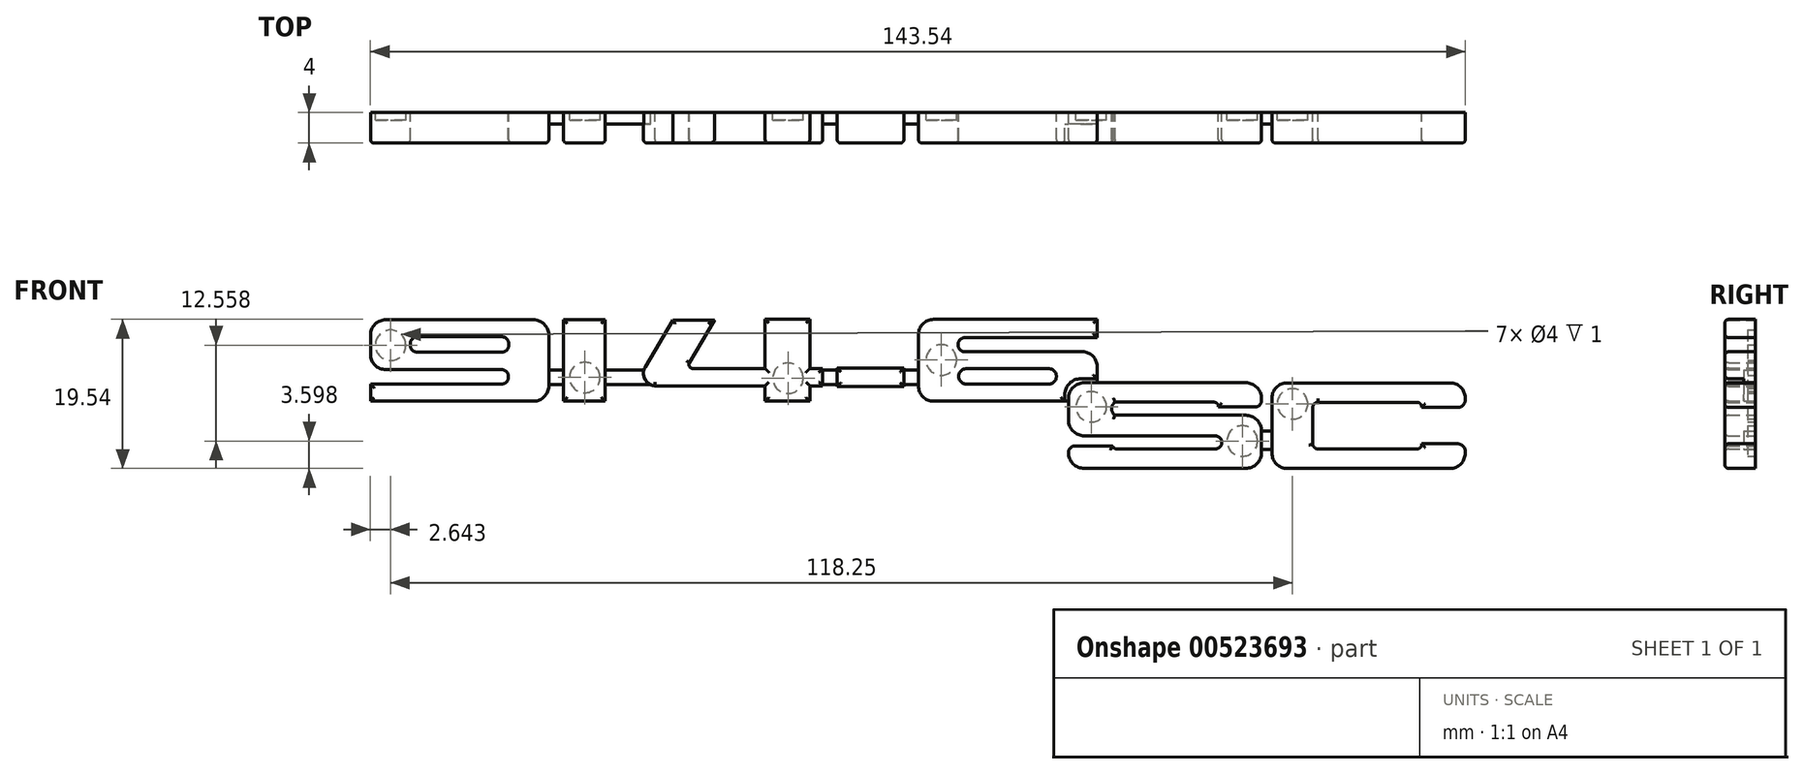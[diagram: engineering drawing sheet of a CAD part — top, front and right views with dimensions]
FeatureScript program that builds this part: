
annotation { "Feature Type Name" : "Feature", "Feature Type Description" : "" }
export const myFeature = defineFeature(function(context is Context, id is Id, definition is map)
    precondition{}
    {
        {
            var Q0;
            Q0=qCreatedBy(makeId("Front.planeOp"),FACE);
            var sketch = newSketch(context, id + "F0", { "sketchPlane" : qUnion([Q0])});
            skLineSegment(sketch, "E0.bottom", {"start": v(-66.52, 34.25) * mm, "end": v(-47.14, 34.25) * mm});
            skLineSegment(sketch, "E0.top", {"start": v(-68.52, 23.57) * mm, "end": v(-47.14, 23.57) * mm});
            skLineSegment(sketch, "E0.left", {"start": v(-68.52, 32.25) * mm, "end": v(-68.52, 29.72) * mm});
            skLineSegment(sketch, "E0.right", {"start": v(-45.14, 32.25) * mm, "end": v(-45.14, 25.57) * mm});
            skPoint(sketch, "E1.visualSharp", {"position": v(-68.52, 34.25) * mm});
            skArc(sketch, "E1.filletArc", {"start": v(-66.52, 34.25) * mm, "mid": v(-67.93, 33.67) * mm, "end": v(-68.52, 32.25) * mm});
            skLineSegment(sketch, "E2", {"start": v(-66.52, 27.72) * mm, "end": v(-51.34, 27.72) * mm});
            skLineSegment(sketch, "E3", {"start": v(-50.44, 26.81) * mm, "end": v(-50.44, 26.71) * mm});
            skLineSegment(sketch, "E4", {"start": v(-51.34, 25.81) * mm, "end": v(-68.52, 25.81) * mm});
            skLineSegment(sketch, "E5.bottom", {"start": v(-62.39, 32.02) * mm, "end": v(-51.29, 32.02) * mm});
            skLineSegment(sketch, "E5.top", {"start": v(-62.39, 30) * mm, "end": v(-51.29, 30) * mm});
            skLineSegment(sketch, "E5.left", {"start": v(-63.3, 31.12) * mm, "end": v(-63.3, 30.91) * mm});
            skLineSegment(sketch, "E5.right", {"start": v(-50.39, 31.12) * mm, "end": v(-50.39, 30.91) * mm});
            skLineSegment(sketch, "E6.trimOffspring", {"start": v(-68.52, 25.81) * mm, "end": v(-68.52, 23.57) * mm});
            skPoint(sketch, "E7.visualSharp", {"position": v(-68.52, 27.72) * mm});
            skArc(sketch, "E7.filletArc", {"start": v(-68.52, 29.72) * mm, "mid": v(-67.93, 28.3) * mm, "end": v(-66.52, 27.72) * mm});
            skPoint(sketch, "E8.visualSharp", {"position": v(-50.44, 27.72) * mm});
            skArc(sketch, "E8.filletArc", {"start": v(-50.44, 26.81) * mm, "mid": v(-50.7, 27.45) * mm, "end": v(-51.34, 27.72) * mm});
            skPoint(sketch, "E9.visualSharp", {"position": v(-50.44, 25.81) * mm});
            skArc(sketch, "E9.filletArc", {"start": v(-51.34, 25.81) * mm, "mid": v(-50.7, 26.08) * mm, "end": v(-50.44, 26.71) * mm});
            skPoint(sketch, "E10.visualSharp", {"position": v(-63.3, 32.02) * mm});
            skArc(sketch, "E10.filletArc", {"start": v(-62.39, 32.02) * mm, "mid": v(-63.03, 31.75) * mm, "end": v(-63.3, 31.12) * mm});
            skPoint(sketch, "E11.visualSharp", {"position": v(-63.3, 30) * mm});
            skArc(sketch, "E11.filletArc", {"start": v(-63.3, 30.91) * mm, "mid": v(-63.03, 30.27) * mm, "end": v(-62.39, 30) * mm});
            skPoint(sketch, "E12.visualSharp", {"position": v(-50.39, 32.02) * mm});
            skArc(sketch, "E12.filletArc", {"start": v(-50.39, 31.12) * mm, "mid": v(-50.65, 31.75) * mm, "end": v(-51.29, 32.02) * mm});
            skPoint(sketch, "E13.visualSharp", {"position": v(-50.39, 30) * mm});
            skArc(sketch, "E13.filletArc", {"start": v(-51.29, 30) * mm, "mid": v(-50.65, 30.27) * mm, "end": v(-50.39, 30.91) * mm});
            skPoint(sketch, "E14.visualSharp", {"position": v(-45.14, 34.25) * mm});
            skArc(sketch, "E14.filletArc", {"start": v(-45.14, 32.25) * mm, "mid": v(-45.72, 33.67) * mm, "end": v(-47.14, 34.25) * mm});
            skPoint(sketch, "E15.visualSharp", {"position": v(-45.14, 23.57) * mm});
            skArc(sketch, "E15.filletArc", {"start": v(-47.14, 23.57) * mm, "mid": v(-45.72, 24.16) * mm, "end": v(-45.14, 25.57) * mm});
            skLineSegment(sketch, "E16.bottom", {"start": v(-43.22, 34.26) * mm, "end": v(-37.74, 34.26) * mm});
            skLineSegment(sketch, "E16.top", {"start": v(-43.22, 23.58) * mm, "end": v(-37.74, 23.58) * mm});
            skLineSegment(sketch, "E16.left", {"start": v(-43.22, 34.26) * mm, "end": v(-43.22, 23.58) * mm});
            skLineSegment(sketch, "E16.right", {"start": v(-37.74, 34.26) * mm, "end": v(-37.74, 23.58) * mm});
            skLineSegment(sketch, "E17.bottom", {"start": v(-10.91, 34.3) * mm, "end": v(-16.77, 34.3) * mm});
            skLineSegment(sketch, "E17.top", {"start": v(-10.91, 23.58) * mm, "end": v(-16.77, 23.58) * mm});
            skLineSegment(sketch, "E17.left", {"start": v(-10.91, 34.3) * mm, "end": v(-10.91, 27.87) * mm});
            skLineSegment(sketch, "E17.right", {"start": v(-16.77, 34.3) * mm, "end": v(-16.77, 27.87) * mm});
            skLineSegment(sketch, "E18.bottom", {"start": v(-9.22, 27.87) * mm, "end": v(-10.91, 27.87) * mm});
            skLineSegment(sketch, "E18.top", {"start": v(-9.22, 25.6) * mm, "end": v(-10.91, 25.6) * mm});
            skLineSegment(sketch, "E18.left", {"start": v(-9.22, 27.87) * mm, "end": v(-9.22, 25.6) * mm});
            skLineSegment(sketch, "E19.trimOffspring", {"start": v(-16.77, 27.87) * mm, "end": v(-26.26, 27.87) * mm});
            skLineSegment(sketch, "E20.trimOffspring", {"start": v(-10.91, 25.6) * mm, "end": v(-10.91, 23.58) * mm});
            skLineSegment(sketch, "E21.trimOffspring", {"start": v(-16.77, 25.6) * mm, "end": v(-26.26, 25.6) * mm});
            skLineSegment(sketch, "E22.trimOffspring", {"start": v(-16.77, 25.6) * mm, "end": v(-16.77, 23.58) * mm});
            skLineSegment(sketch, "E23", {"start": v(-23.37, 34.22) * mm, "end": v(-28.86, 34.22) * mm});
            skLineSegment(sketch, "E24", {"start": v(-23.37, 34.22) * mm, "end": v(-26.68, 28.6) * mm});
            skLineSegment(sketch, "E25", {"start": v(-28.86, 34.22) * mm, "end": v(-32.5, 28.07) * mm});
            skLineSegment(sketch, "E26", {"start": v(-26.26, 25.6) * mm, "end": v(-31.22, 25.6) * mm});
            skArc(sketch, "E27", {"start": v(-32.5, 28.07) * mm, "mid": v(-32.54, 26.48) * mm, "end": v(-31.22, 25.6) * mm});
            skArc(sketch, "E28", {"start": v(-26.68, 28.6) * mm, "mid": v(-26.69, 28.12) * mm, "end": v(-26.26, 27.87) * mm});
            skLineSegment(sketch, "E29.bottom", {"start": v(-7.32, 27.9) * mm, "end": v(1.42, 27.9) * mm});
            skLineSegment(sketch, "E29.top", {"start": v(-7.32, 25.5) * mm, "end": v(1.42, 25.5) * mm});
            skLineSegment(sketch, "E29.left", {"start": v(-7.32, 27.9) * mm, "end": v(-7.32, 25.5) * mm});
            skLineSegment(sketch, "E29.right", {"start": v(1.42, 27.9) * mm, "end": v(1.42, 25.5) * mm});
            skLineSegment(sketch, "E30.bottom", {"start": v(26.75, 34.3) * mm, "end": v(5.33, 34.3) * mm});
            skLineSegment(sketch, "E30.top", {"start": v(22.52, 23.57) * mm, "end": v(5.33, 23.57) * mm});
            skLineSegment(sketch, "E30.left", {"start": v(26.75, 34.3) * mm, "end": v(26.75, 31.9) * mm});
            skLineSegment(sketch, "E30.right", {"start": v(3.33, 32.3) * mm, "end": v(3.33, 25.57) * mm});
            skPoint(sketch, "E31.visualSharp", {"position": v(3.33, 34.3) * mm});
            skArc(sketch, "E31.filletArc", {"start": v(5.33, 34.3) * mm, "mid": v(3.91, 33.71) * mm, "end": v(3.33, 32.3) * mm});
            skPoint(sketch, "E32.visualSharp", {"position": v(3.33, 23.57) * mm});
            skArc(sketch, "E32.filletArc", {"start": v(3.33, 25.57) * mm, "mid": v(3.91, 24.16) * mm, "end": v(5.33, 23.57) * mm});
            skLineSegment(sketch, "E33", {"start": v(26.75, 31.9) * mm, "end": v(9.44, 31.9) * mm});
            skLineSegment(sketch, "E34", {"start": v(9.44, 30.06) * mm, "end": v(24.83, 30.06) * mm});
            skLineSegment(sketch, "E35.bottom", {"start": v(9.61, 27.84) * mm, "end": v(20.42, 27.84) * mm});
            skLineSegment(sketch, "E35.top", {"start": v(9.61, 25.82) * mm, "end": v(20.42, 25.82) * mm});
            skLineSegment(sketch, "E35.left", {"start": v(8.61, 26.84) * mm, "end": v(8.61, 26.82) * mm});
            skLineSegment(sketch, "E35.right", {"start": v(21.42, 26.84) * mm, "end": v(21.42, 26.82) * mm});
            skPoint(sketch, "E36.visualSharp", {"position": v(8.61, 27.84) * mm});
            skArc(sketch, "E36.filletArc", {"start": v(9.61, 27.84) * mm, "mid": v(8.9, 27.54) * mm, "end": v(8.61, 26.84) * mm});
            skPoint(sketch, "E37.visualSharp", {"position": v(8.61, 25.82) * mm});
            skArc(sketch, "E37.filletArc", {"start": v(8.61, 26.82) * mm, "mid": v(8.9, 26.12) * mm, "end": v(9.61, 25.82) * mm});
            skPoint(sketch, "E38.visualSharp", {"position": v(27.42, 23.74) * mm});
            skArc(sketch, "E38.filletArc", {"start": v(21.42, 26.84) * mm, "mid": v(21.13, 27.54) * mm, "end": v(20.42, 27.84) * mm});
            skPoint(sketch, "E39.visualSharp", {"position": v(21.5, 24.83) * mm});
            skArc(sketch, "E39.filletArc", {"start": v(20.42, 25.82) * mm, "mid": v(21.13, 26.12) * mm, "end": v(21.42, 26.82) * mm});
            skArc(sketch, "E40", {"start": v(9.44, 31.9) * mm, "mid": v(8.52, 30.98) * mm, "end": v(9.44, 30.06) * mm});
            skLineSegment(sketch, "E41.trimOffspring", {"start": v(26.75, 28.14) * mm, "end": v(26.75, 26.52) * mm});
            skPoint(sketch, "E42.visualSharp", {"position": v(26.75, 30.06) * mm});
            skArc(sketch, "E42.filletArc", {"start": v(26.75, 28.14) * mm, "mid": v(26.19, 29.5) * mm, "end": v(24.83, 30.06) * mm});
            skLineSegment(sketch, "E43", {"start": v(22.52, 23.57) * mm, "end": v(22.52, 24.42) * mm});
            skLineSegment(sketch, "E44", {"start": v(24.62, 26.52) * mm, "end": v(26.75, 26.52) * mm});
            skPoint(sketch, "E45.visualSharp", {"position": v(22.6, 25.53) * mm});
            skArc(sketch, "E45.filletArc", {"start": v(24.62, 26.52) * mm, "mid": v(23.13, 25.9) * mm, "end": v(22.52, 24.42) * mm});
            skPoint(sketch, "E46.firstSnap0", {"position": v(21.13, 26.12) * mm});
            skLineSegment(sketch, "E46.bottom", {"start": v(46.22, 26) * mm, "end": v(40.34, 26) * mm});
            skLineSegment(sketch, "E46.top", {"start": v(46.22, 14.76) * mm, "end": v(40.34, 14.76) * mm});
            skLineSegment(sketch, "E46.left", {"start": v(48.32, 23.9) * mm, "end": v(48.32, 23.65) * mm});
            skLineSegment(sketch, "E46.right", {"start": v(23, 23.9) * mm, "end": v(23, 21.11) * mm});
            skPoint(sketch, "E47.visualSharp", {"position": v(23, 26) * mm});
            skArc(sketch, "E47.filletArc", {"start": v(25.1, 26) * mm, "mid": v(23.61, 25.38) * mm, "end": v(23, 23.9) * mm});
            skPoint(sketch, "E48.visualSharp", {"position": v(22.6, 11.98) * mm});
            skArc(sketch, "E48.filletArc", {"start": v(48.32, 23.9) * mm, "mid": v(47.7, 25.38) * mm, "end": v(46.22, 26) * mm});
            skPoint(sketch, "E49.visualSharp", {"position": v(49.1, 15.16) * mm});
            skArc(sketch, "E49.filletArc", {"start": v(46.22, 14.76) * mm, "mid": v(47.7, 15.37) * mm, "end": v(48.32, 16.86) * mm});
            skPoint(sketch, "E50.visualSharp", {"position": v(23, 14.76) * mm});
            skArc(sketch, "E50.filletArc", {"start": v(23, 16.86) * mm, "mid": v(23.61, 15.37) * mm, "end": v(25.1, 14.76) * mm});
            skLineSegment(sketch, "E51", {"start": v(25.08, 19.03) * mm, "end": v(30.91, 19.03) * mm});
            skLineSegment(sketch, "E52", {"start": v(42.24, 17.3) * mm, "end": v(40.34, 17.3) * mm});
            skLineSegment(sketch, "E53", {"start": v(28.8, 17.7) * mm, "end": v(23.84, 17.7) * mm});
            skLineSegment(sketch, "E54", {"start": v(29.07, 21.73) * mm, "end": v(30.91, 21.73) * mm});
            skLineSegment(sketch, "E55", {"start": v(47.48, 22.82) * mm, "end": v(42.67, 22.82) * mm});
            skLineSegment(sketch, "E56", {"start": v(42.07, 23.45) * mm, "end": v(40.34, 23.45) * mm});
            skArc(sketch, "E57", {"start": v(29.1, 23.45) * mm, "mid": v(28.67, 22.6) * mm, "end": v(29.07, 21.73) * mm});
            skPoint(sketch, "E58.end.orphan", {"position": v(42.67, 23.45) * mm});
            skArc(sketch, "E59", {"start": v(42.67, 22.82) * mm, "mid": v(42.5, 23.26) * mm, "end": v(42.07, 23.45) * mm});
            skArc(sketch, "E60", {"start": v(28.8, 17.7) * mm, "mid": v(29.01, 17.41) * mm, "end": v(29.35, 17.3) * mm});
            skLineSegment(sketch, "E61.trimOffspring", {"start": v(23, 16.86) * mm, "end": v(23, 16.85) * mm});
            skPoint(sketch, "E62.visualSharp", {"position": v(23, 17.7) * mm});
            skArc(sketch, "E62.filletArc", {"start": v(23.84, 17.7) * mm, "mid": v(23.25, 17.45) * mm, "end": v(23, 16.85) * mm});
            skPoint(sketch, "E63.visualSharp", {"position": v(23, 19.03) * mm});
            skArc(sketch, "E63.filletArc", {"start": v(23, 21.11) * mm, "mid": v(23.6, 19.64) * mm, "end": v(25.08, 19.03) * mm});
            skLineSegment(sketch, "E64.trimOffspring", {"start": v(48.32, 19.65) * mm, "end": v(48.32, 16.86) * mm});
            skPoint(sketch, "E65.visualSharp", {"position": v(49.1, 22.93) * mm});
            skArc(sketch, "E65.filletArc", {"start": v(47.48, 22.82) * mm, "mid": v(48.07, 23.06) * mm, "end": v(48.32, 23.65) * mm});
            skPoint(sketch, "E66.visualSharp", {"position": v(49.1, 21.7) * mm});
            skArc(sketch, "E66.filletArc", {"start": v(48.32, 19.65) * mm, "mid": v(47.7, 21.12) * mm, "end": v(46.24, 21.73) * mm});
            skLineSegment(sketch, "E67.bottom", {"start": v(51.66, 25.98) * mm, "end": v(57.41, 25.98) * mm});
            skLineSegment(sketch, "E67.top", {"start": v(51.66, 14.76) * mm, "end": v(57.41, 14.76) * mm});
            skLineSegment(sketch, "E67.left", {"start": v(49.68, 24) * mm, "end": v(49.68, 16.74) * mm});
            skLineSegment(sketch, "E68.bottom", {"start": v(68.68, 23.43) * mm, "end": v(66.84, 23.43) * mm});
            skLineSegment(sketch, "E68.top", {"start": v(68.69, 17.3) * mm, "end": v(66.84, 17.3) * mm});
            skLineSegment(sketch, "E69", {"start": v(55.03, 18) * mm, "end": v(55.03, 22.74) * mm});
            skArc(sketch, "E70", {"start": v(69.32, 22.74) * mm, "mid": v(69.15, 23.22) * mm, "end": v(68.68, 23.43) * mm});
            skPoint(sketch, "E71.visualSharp", {"position": v(75.02, 17.93) * mm});
            skPoint(sketch, "E72.visualSharp", {"position": v(75.02, 14.93) * mm});
            skArc(sketch, "E72.filletArc", {"start": v(73.04, 14.76) * mm, "mid": v(74.44, 15.34) * mm, "end": v(75.02, 16.74) * mm});
            skPoint(sketch, "E73.visualSharp", {"position": v(48.52, 12.25) * mm});
            skArc(sketch, "E73.filletArc", {"start": v(75.02, 24) * mm, "mid": v(74.44, 25.4) * mm, "end": v(73.04, 25.98) * mm});
            skPoint(sketch, "E74.visualSharp", {"position": v(23.18, 12.25) * mm});
            skArc(sketch, "E74.filletArc", {"start": v(51.66, 25.98) * mm, "mid": v(50.26, 25.4) * mm, "end": v(49.68, 24) * mm});
            skPoint(sketch, "E75.visualSharp", {"position": v(49.68, 14.76) * mm});
            skArc(sketch, "E75.filletArc", {"start": v(49.68, 16.74) * mm, "mid": v(50.26, 15.34) * mm, "end": v(51.66, 14.76) * mm});
            skArc(sketch, "E76", {"start": v(55.72, 23.43) * mm, "mid": v(55.23, 23.23) * mm, "end": v(55.03, 22.74) * mm});
            skLineSegment(sketch, "E77", {"start": v(55.03, 18) * mm, "end": v(55.03, 17.88) * mm});
            skArc(sketch, "E78", {"start": v(55.03, 17.88) * mm, "mid": v(55.27, 17.47) * mm, "end": v(55.72, 17.3) * mm});
            skLineSegment(sketch, "E79.bottom", {"start": v(3.33, 27.64) * mm, "end": v(1.42, 27.64) * mm});
            skLineSegment(sketch, "E79.top", {"start": v(3.33, 25.76) * mm, "end": v(1.42, 25.76) * mm});
            skLineSegment(sketch, "E79.left", {"start": v(3.33, 27.64) * mm, "end": v(3.33, 25.76) * mm});
            skLineSegment(sketch, "E80.trimOffspring", {"start": v(-7.32, 27.64) * mm, "end": v(-9.22, 27.64) * mm});
            skLineSegment(sketch, "E81.trimOffspring", {"start": v(-7.32, 25.76) * mm, "end": v(-9.22, 25.76) * mm});
            skLineSegment(sketch, "E82", {"start": v(-31.8, 25.76) * mm, "end": v(-33.56, 25.76) * mm});
            skLineSegment(sketch, "E83", {"start": v(-32.67, 27.64) * mm, "end": v(-33.56, 27.64) * mm});
            skLineSegment(sketch, "E84", {"start": v(-33.56, 27.64) * mm, "end": v(-37.74, 27.64) * mm});
            skLineSegment(sketch, "E85", {"start": v(-33.56, 25.76) * mm, "end": v(-37.74, 25.76) * mm});
            skLineSegment(sketch, "E86.trimOffspring", {"start": v(-43.22, 27.64) * mm, "end": v(-45.14, 27.64) * mm});
            skLineSegment(sketch, "E87.trimOffspring", {"start": v(-43.22, 25.76) * mm, "end": v(-45.14, 25.76) * mm});
            skPoint(sketch, "E88.end.orphan", {"position": v(49.68, 19.46) * mm});
            skPoint(sketch, "E89.end.orphan", {"position": v(49.68, 17.09) * mm});
            skArc(sketch, "E90", {"start": v(42.24, 17.3) * mm, "mid": v(43.1, 18.17) * mm, "end": v(42.24, 19.03) * mm});
            skLineSegment(sketch, "E91.top", {"start": v(69.32, 18) * mm, "end": v(74.02, 18) * mm});
            skArc(sketch, "E92", {"start": v(68.69, 17.3) * mm, "mid": v(69.15, 17.51) * mm, "end": v(69.32, 18) * mm});
            skPoint(sketch, "E93.trimOffspring.start.orphan", {"position": v(75.02, 17.07) * mm});
            skLineSegment(sketch, "E94", {"start": v(75.02, 16.74) * mm, "end": v(75.02, 17) * mm});
            skLineSegment(sketch, "E95", {"start": v(69.32, 22.74) * mm, "end": v(74.02, 22.74) * mm});
            skLineSegment(sketch, "E96", {"start": v(75.02, 24) * mm, "end": v(75.02, 23.74) * mm});
            skPoint(sketch, "E97.visualSharp", {"position": v(75.02, 22.74) * mm});
            skArc(sketch, "E97.filletArc", {"start": v(74.02, 22.74) * mm, "mid": v(74.73, 23.04) * mm, "end": v(75.02, 23.74) * mm});
            skPoint(sketch, "E98.visualSharp", {"position": v(75.02, 18) * mm});
            skArc(sketch, "E98.filletArc", {"start": v(75.02, 17) * mm, "mid": v(74.73, 17.7) * mm, "end": v(74.02, 18) * mm});
            skLineSegment(sketch, "E99.trimOffspring", {"start": v(30.91, 26) * mm, "end": v(25.1, 26) * mm});
            skLineSegment(sketch, "E100.trimOffspring", {"start": v(30.91, 23.45) * mm, "end": v(29.1, 23.45) * mm});
            skLineSegment(sketch, "E101.trimOffspring", {"start": v(40.34, 21.73) * mm, "end": v(46.24, 21.73) * mm});
            skLineSegment(sketch, "E102.trimOffspring", {"start": v(40.34, 19.03) * mm, "end": v(42.24, 19.03) * mm});
            skLineSegment(sketch, "E103.trimOffspring", {"start": v(30.91, 17.3) * mm, "end": v(29.35, 17.3) * mm});
            skLineSegment(sketch, "E104.trimOffspring", {"start": v(30.91, 14.76) * mm, "end": v(25.1, 14.76) * mm});
            skLineSegment(sketch, "E105.trimOffspring", {"start": v(66.84, 25.98) * mm, "end": v(73.04, 25.98) * mm});
            skLineSegment(sketch, "E106.trimOffspring", {"start": v(57.41, 23.43) * mm, "end": v(55.72, 23.43) * mm});
            skLineSegment(sketch, "E107.trimOffspring", {"start": v(57.41, 17.3) * mm, "end": v(55.72, 17.3) * mm});
            skLineSegment(sketch, "E108.trimOffspring", {"start": v(66.84, 14.76) * mm, "end": v(73.04, 14.76) * mm});
            skLineSegment(sketch, "E109", {"start": v(30.91, 26) * mm, "end": v(40.34, 26) * mm});
            skLineSegment(sketch, "E110", {"start": v(30.91, 23.45) * mm, "end": v(40.34, 23.45) * mm});
            skLineSegment(sketch, "E111", {"start": v(30.91, 21.73) * mm, "end": v(40.34, 21.73) * mm});
            skLineSegment(sketch, "E112", {"start": v(30.91, 19.03) * mm, "end": v(40.34, 19.03) * mm});
            skLineSegment(sketch, "E113", {"start": v(30.91, 17.3) * mm, "end": v(40.34, 17.3) * mm});
            skLineSegment(sketch, "E114", {"start": v(30.91, 14.76) * mm, "end": v(40.34, 14.76) * mm});
            skLineSegment(sketch, "E115", {"start": v(57.41, 25.98) * mm, "end": v(66.84, 25.98) * mm});
            skLineSegment(sketch, "E116", {"start": v(57.41, 23.43) * mm, "end": v(66.84, 23.43) * mm});
            skLineSegment(sketch, "E117", {"start": v(57.41, 17.3) * mm, "end": v(66.84, 17.3) * mm});
            skLineSegment(sketch, "E118", {"start": v(57.41, 14.76) * mm, "end": v(66.84, 14.76) * mm});
            skLineSegment(sketch, "E119", {"start": v(26.75, 26.52) * mm, "end": v(26.75, 26) * mm});
            skLineSegment(sketch, "E120", {"start": v(22.52, 23.57) * mm, "end": v(23, 23.57) * mm});
            skLineSegment(sketch, "E121", {"start": v(48.32, 17.24) * mm, "end": v(49.68, 17.24) * mm});
            skLineSegment(sketch, "E122", {"start": v(48.32, 19.65) * mm, "end": v(49.68, 19.65) * mm});
            skSolve(sketch);
        }
        {
            var Q0;
            {var subQ0=sQuery(id+"F0.wireOp",EDGE,"E86.trimOffspring");Q0=makeQuery(id+"F0.imprint","IMPRINT",FACE,{"disambiguationData":[TD([[makeQuery(id+"F0.imprint","IMPRINT",EDGE,{"derivedFrom":subQ0}),1.0]])]});}
            var Q1;
            {var subQ1=sQuery(id+"F0.wireOp",EDGE,"E82");Q1=makeQuery(id+"F0.imprint","IMPRINT",FACE,{"disambiguationData":[TD([[makeQuery(id+"F0.imprint","IMPRINT",EDGE,{"derivedFrom":subQ1}),-1.0]])]});}
            var Q2;
            {var subQ0=sQuery(id+"F0.wireOp",EDGE,"E80.trimOffspring");Q2=makeQuery(id+"F0.imprint","IMPRINT",FACE,{"disambiguationData":[TD([[makeQuery(id+"F0.imprint","IMPRINT",EDGE,{"derivedFrom":subQ0}),1.0]])]});}
            var Q3;
            {var subQ0=sQuery(id+"F0.wireOp",EDGE,"E79.bottom");Q3=makeQuery(id+"F0.imprint","IMPRINT",FACE,{"disambiguationData":[TD([[makeQuery(id+"F0.imprint","IMPRINT",EDGE,{"derivedFrom":subQ0}),1.0]])]});}
            var Q4;
            Q4=makeQuery(id+"F0.imprint","IMPRINT",FACE,{"disambiguationData":[TD([[makeQuery(id+"F0.imprint","IMPRINT",EDGE,{"derivedFrom":sQuery(id+"F0.wireOp",EDGE,"E64.trimOffspring")}),1.0]])]});
            var Q5;
            Q5=makeQuery(id+"F0.imprint","IMPRINT",FACE,{"disambiguationData":[TD([[makeQuery(id+"F0.imprint","IMPRINT",EDGE,{"derivedFrom":sQuery(id+"F0.wireOp",EDGE,"E43")}),-1.0]])]});
            extrude(context, id + "F1", {"entities" : qUnion([Q0, Q1, Q2, Q3, Q4, Q5]), "depth" : 1.5 * mm, "offsetDistance" : 25 * mm});
        }
        {
            var Q0;
            Q0=makeQuery(id+"F0.imprint","IMPRINT",FACE,{"disambiguationData":[TD([[makeQuery(id+"F0.imprint","IMPRINT",EDGE,{"derivedFrom":sQuery(id+"F0.wireOp",EDGE,"E0.bottom")}),-1.0]])]});
            var Q1;
            {var subQ3=sQuery(id+"F0.wireOp",EDGE,"E16.bottom");Q1=makeQuery(id+"F0.imprint","IMPRINT",FACE,{"disambiguationData":[TD([[makeQuery(id+"F0.imprint","IMPRINT",EDGE,{"derivedFrom":subQ3}),-1.0]])]});}
            var Q2;
            Q2=makeQuery(id+"F0.imprint","IMPRINT",FACE,{"disambiguationData":[TD([[makeQuery(id+"F0.imprint","IMPRINT",EDGE,{"derivedFrom":sQuery(id+"F0.wireOp",EDGE,"E17.bottom")}),1.0]])]});
            var Q3;
            {var subQ3=sQuery(id+"F0.wireOp",EDGE,"E29.bottom");Q3=makeQuery(id+"F0.imprint","IMPRINT",FACE,{"disambiguationData":[TD([[makeQuery(id+"F0.imprint","IMPRINT",EDGE,{"derivedFrom":subQ3}),-1.0]])]});}
            var Q4;
            Q4=makeQuery(id+"F0.imprint","IMPRINT",FACE,{"disambiguationData":[TD([[makeQuery(id+"F0.imprint","IMPRINT",EDGE,{"derivedFrom":sQuery(id+"F0.wireOp",EDGE,"E30.bottom")}),1.0]])]});
            var Q5;
            Q5=makeQuery(id+"F0.imprint","IMPRINT",FACE,{"disambiguationData":[TD([[makeQuery(id+"F0.imprint","IMPRINT",EDGE,{"derivedFrom":sQuery(id+"F0.wireOp",EDGE,"E46.top")}),-1.0]])]});
            var Q6;
            Q6=makeQuery(id+"F0.imprint","IMPRINT",FACE,{"disambiguationData":[TD([[makeQuery(id+"F0.imprint","IMPRINT",EDGE,{"derivedFrom":sQuery(id+"F0.wireOp",EDGE,"E67.bottom")}),-1.0]])]});
            extrude(context, id + "F2", {"entities" : qUnion([Q0, Q1, Q2, Q3, Q4, Q5, Q6]), "depth" : 4 * mm, "offsetDistance" : 25 * mm});
        }
        {
            var Q0;
            Q0=makeQuery(id+"F1.opExtrude","SWEPT_BODY",BODY,{"disambiguationData":[OSD([sQuery(id+"F0.wireOp",EDGE,"E0.right"),sQuery(id+"F0.wireOp",EDGE,"E16.left"),sQuery(id+"F0.wireOp",EDGE,"E86.trimOffspring"),sQuery(id+"F0.wireOp",EDGE,"E87.trimOffspring")])]});
            var Q1;
            Q1=makeQuery(id+"F1.opExtrude","SWEPT_BODY",BODY,{"disambiguationData":[OSD([sQuery(id+"F0.wireOp",EDGE,"E16.right"),sQuery(id+"F0.wireOp",EDGE,"E27"),sQuery(id+"F0.wireOp",EDGE,"E82"),sQuery(id+"F0.wireOp",EDGE,"E83"),sQuery(id+"F0.wireOp",EDGE,"E84"),sQuery(id+"F0.wireOp",EDGE,"E85")])]});
            var Q2;
            Q2=makeQuery(id+"F1.opExtrude","SWEPT_BODY",BODY,{"disambiguationData":[OSD([sQuery(id+"F0.wireOp",EDGE,"E18.left"),sQuery(id+"F0.wireOp",EDGE,"E29.left"),sQuery(id+"F0.wireOp",EDGE,"E80.trimOffspring"),sQuery(id+"F0.wireOp",EDGE,"E81.trimOffspring")])]});
            var Q3;
            Q3=makeQuery(id+"F1.opExtrude","SWEPT_BODY",BODY,{"disambiguationData":[OSD([sQuery(id+"F0.wireOp",EDGE,"E29.right"),sQuery(id+"F0.wireOp",EDGE,"E79.bottom"),sQuery(id+"F0.wireOp",EDGE,"E79.top"),sQuery(id+"F0.wireOp",EDGE,"E79.left")])]});
            var Q4;
            Q4=makeQuery(id+"F1.opExtrude","SWEPT_BODY",BODY,{"disambiguationData":[OSD([sQuery(id+"F0.wireOp",EDGE,"E43"),sQuery(id+"F0.wireOp",EDGE,"E44"),sQuery(id+"F0.wireOp",EDGE,"E45.filletArc"),sQuery(id+"F0.wireOp",EDGE,"E46.bottom"),sQuery(id+"F0.wireOp",EDGE,"E46.right"),sQuery(id+"F0.wireOp",EDGE,"E47.filletArc"),sQuery(id+"F0.wireOp",EDGE,"XMzfFIXU-IzKp-9okF-d4nS-TtUoLVSPwyGc"),sQuery(id+"F0.wireOp",EDGE,"e7Qd8Rkx-YhGh-OuG7-C6sY-1t4VXorSgqZP")])]});
            var Q5;
            Q5=makeQuery(id+"F1.opExtrude","SWEPT_BODY",BODY,{"disambiguationData":[OSD([sQuery(id+"F0.wireOp",EDGE,"E64.trimOffspring"),sQuery(id+"F0.wireOp",EDGE,"E67.left"),sQuery(id+"F0.wireOp",EDGE,"E89"),sQuery(id+"F0.wireOp",EDGE,"E88")])]});
            var Q6;
            Q6=makeQuery(id+"F2.opExtrude","SWEPT_BODY",BODY,{"disambiguationData":[OSD([sQuery(id+"F0.wireOp",EDGE,"E0.bottom"),sQuery(id+"F0.wireOp",EDGE,"E0.top"),sQuery(id+"F0.wireOp",EDGE,"E0.left"),sQuery(id+"F0.wireOp",EDGE,"E0.right"),sQuery(id+"F0.wireOp",EDGE,"E1.filletArc"),sQuery(id+"F0.wireOp",EDGE,"E2"),sQuery(id+"F0.wireOp",EDGE,"E3"),sQuery(id+"F0.wireOp",EDGE,"E4"),sQuery(id+"F0.wireOp",EDGE,"E5.bottom"),sQuery(id+"F0.wireOp",EDGE,"E5.top"),sQuery(id+"F0.wireOp",EDGE,"E5.left"),sQuery(id+"F0.wireOp",EDGE,"E5.right"),sQuery(id+"F0.wireOp",EDGE,"E6.trimOffspring"),sQuery(id+"F0.wireOp",EDGE,"E7.filletArc"),sQuery(id+"F0.wireOp",EDGE,"E8.filletArc"),sQuery(id+"F0.wireOp",EDGE,"E9.filletArc"),sQuery(id+"F0.wireOp",EDGE,"E10.filletArc"),sQuery(id+"F0.wireOp",EDGE,"E11.filletArc"),sQuery(id+"F0.wireOp",EDGE,"E12.filletArc"),sQuery(id+"F0.wireOp",EDGE,"E13.filletArc"),sQuery(id+"F0.wireOp",EDGE,"E14.filletArc"),sQuery(id+"F0.wireOp",EDGE,"E15.filletArc")])]});
            var Q7;
            Q7=makeQuery(id+"F2.opExtrude","SWEPT_BODY",BODY,{"disambiguationData":[OSD([sQuery(id+"F0.wireOp",EDGE,"E16.bottom"),sQuery(id+"F0.wireOp",EDGE,"E16.top"),sQuery(id+"F0.wireOp",EDGE,"E16.left"),sQuery(id+"F0.wireOp",EDGE,"E16.right")])]});
            var Q8;
            Q8=makeQuery(id+"F2.opExtrude","SWEPT_BODY",BODY,{"disambiguationData":[OSD([sQuery(id+"F0.wireOp",EDGE,"E17.bottom"),sQuery(id+"F0.wireOp",EDGE,"E17.top"),sQuery(id+"F0.wireOp",EDGE,"E17.left"),sQuery(id+"F0.wireOp",EDGE,"E17.right"),sQuery(id+"F0.wireOp",EDGE,"E18.bottom"),sQuery(id+"F0.wireOp",EDGE,"E18.top"),sQuery(id+"F0.wireOp",EDGE,"E18.left"),sQuery(id+"F0.wireOp",EDGE,"E19.trimOffspring"),sQuery(id+"F0.wireOp",EDGE,"E20.trimOffspring"),sQuery(id+"F0.wireOp",EDGE,"E21.trimOffspring"),sQuery(id+"F0.wireOp",EDGE,"E22.trimOffspring"),sQuery(id+"F0.wireOp",EDGE,"E23"),sQuery(id+"F0.wireOp",EDGE,"E24"),sQuery(id+"F0.wireOp",EDGE,"E25"),sQuery(id+"F0.wireOp",EDGE,"E26"),sQuery(id+"F0.wireOp",EDGE,"E27"),sQuery(id+"F0.wireOp",EDGE,"E28")])]});
            var Q9;
            Q9=makeQuery(id+"F2.opExtrude","SWEPT_BODY",BODY,{"disambiguationData":[OSD([sQuery(id+"F0.wireOp",EDGE,"E29.bottom"),sQuery(id+"F0.wireOp",EDGE,"E29.top"),sQuery(id+"F0.wireOp",EDGE,"E29.left"),sQuery(id+"F0.wireOp",EDGE,"E29.right")])]});
            var Q10;
            Q10=makeQuery(id+"F2.opExtrude","SWEPT_BODY",BODY,{"disambiguationData":[OSD([sQuery(id+"F0.wireOp",EDGE,"E30.bottom"),sQuery(id+"F0.wireOp",EDGE,"E30.top"),sQuery(id+"F0.wireOp",EDGE,"E30.left"),sQuery(id+"F0.wireOp",EDGE,"E30.right"),sQuery(id+"F0.wireOp",EDGE,"E31.filletArc"),sQuery(id+"F0.wireOp",EDGE,"E32.filletArc"),sQuery(id+"F0.wireOp",EDGE,"E33"),sQuery(id+"F0.wireOp",EDGE,"E34"),sQuery(id+"F0.wireOp",EDGE,"E35.bottom"),sQuery(id+"F0.wireOp",EDGE,"E35.top"),sQuery(id+"F0.wireOp",EDGE,"E35.left"),sQuery(id+"F0.wireOp",EDGE,"E35.right"),sQuery(id+"F0.wireOp",EDGE,"E36.filletArc"),sQuery(id+"F0.wireOp",EDGE,"E37.filletArc"),sQuery(id+"F0.wireOp",EDGE,"E38.filletArc"),sQuery(id+"F0.wireOp",EDGE,"E39.filletArc"),sQuery(id+"F0.wireOp",EDGE,"E40"),sQuery(id+"F0.wireOp",EDGE,"E41.trimOffspring"),sQuery(id+"F0.wireOp",EDGE,"E42.filletArc"),sQuery(id+"F0.wireOp",EDGE,"E43"),sQuery(id+"F0.wireOp",EDGE,"E44"),sQuery(id+"F0.wireOp",EDGE,"E45.filletArc"),sQuery(id+"F0.wireOp",EDGE,"E79.left")])]});
            var Q11;
            Q11=makeQuery(id+"F2.opExtrude","SWEPT_BODY",BODY,{"disambiguationData":[OSD([sQuery(id+"F0.wireOp",EDGE,"E46.bottom"),sQuery(id+"F0.wireOp",EDGE,"E46.top"),sQuery(id+"F0.wireOp",EDGE,"E46.left"),sQuery(id+"F0.wireOp",EDGE,"E46.right"),sQuery(id+"F0.wireOp",EDGE,"E47.filletArc"),sQuery(id+"F0.wireOp",EDGE,"E48.filletArc"),sQuery(id+"F0.wireOp",EDGE,"E49.filletArc"),sQuery(id+"F0.wireOp",EDGE,"E50.filletArc"),sQuery(id+"F0.wireOp",EDGE,"E51"),sQuery(id+"F0.wireOp",EDGE,"E52"),sQuery(id+"F0.wireOp",EDGE,"E53"),sQuery(id+"F0.wireOp",EDGE,"E54"),sQuery(id+"F0.wireOp",EDGE,"E55"),sQuery(id+"F0.wireOp",EDGE,"E56"),sQuery(id+"F0.wireOp",EDGE,"E57"),sQuery(id+"F0.wireOp",EDGE,"DLBRGIPo-igv8-U5Ki-hssD-qP5Wvc2arMu2"),sQuery(id+"F0.wireOp",EDGE,"E59"),sQuery(id+"F0.wireOp",EDGE,"E60"),sQuery(id+"F0.wireOp",EDGE,"E61.trimOffspring"),sQuery(id+"F0.wireOp",EDGE,"E62.filletArc"),sQuery(id+"F0.wireOp",EDGE,"E63.filletArc"),sQuery(id+"F0.wireOp",EDGE,"E64.trimOffspring"),sQuery(id+"F0.wireOp",EDGE,"E65.filletArc"),sQuery(id+"F0.wireOp",EDGE,"E66.filletArc")])]});
            var Q12;
            Q12=makeQuery(id+"F2.opExtrude","SWEPT_BODY",BODY,{"disambiguationData":[OSD([sQuery(id+"F0.wireOp",EDGE,"E67.bottom"),sQuery(id+"F0.wireOp",EDGE,"E67.top"),sQuery(id+"F0.wireOp",EDGE,"E67.left"),sQuery(id+"F0.wireOp",EDGE,"E67.right"),sQuery(id+"F0.wireOp",EDGE,"E68.bottom"),sQuery(id+"F0.wireOp",EDGE,"E68.top"),sQuery(id+"F0.wireOp",EDGE,"W34rrdPF-5A4v-98ez-cMOX-sxhZx3srIAKQ"),sQuery(id+"F0.wireOp",EDGE,"yoT0j4jh-KsDp-Vx2W-hgaE-VbdXvh3J3yn9"),sQuery(id+"F0.wireOp",EDGE,"E69"),sQuery(id+"F0.wireOp",EDGE,"E93.trimOffspring"),sQuery(id+"F0.wireOp",EDGE,"E70"),sQuery(id+"F0.wireOp",EDGE,"FAs5oKjp-0fME-HACK-cPX3-1Olh0WYhMQdt"),sQuery(id+"F0.wireOp",EDGE,"E71.filletArc"),sQuery(id+"F0.wireOp",EDGE,"E72.filletArc"),sQuery(id+"F0.wireOp",EDGE,"E73.filletArc"),sQuery(id+"F0.wireOp",EDGE,"E74.filletArc"),sQuery(id+"F0.wireOp",EDGE,"E75.filletArc"),sQuery(id+"F0.wireOp",EDGE,"E76"),sQuery(id+"F0.wireOp",EDGE,"E77"),sQuery(id+"F0.wireOp",EDGE,"E78")])]});
            booleanBodies(context, id + "F3", {"operationType" : BooleanOperationType.UNION, "tools" : qUnion([Q0, Q1, Q2, Q3, Q4, Q5, Q6, Q7, Q8, Q9, Q10, Q11, Q12])});
        }
        {
            var Q0;
            Q0=makeQuery(id+"F2.opExtrude","CAP_FACE",FACE,{"disambiguationData":[OSD([sQuery(id+"F0.wireOp",EDGE,"E0.bottom"),sQuery(id+"F0.wireOp",EDGE,"E0.top"),sQuery(id+"F0.wireOp",EDGE,"E0.left"),sQuery(id+"F0.wireOp",EDGE,"E0.right"),sQuery(id+"F0.wireOp",EDGE,"E1.filletArc"),sQuery(id+"F0.wireOp",EDGE,"E2"),sQuery(id+"F0.wireOp",EDGE,"E3"),sQuery(id+"F0.wireOp",EDGE,"E4"),sQuery(id+"F0.wireOp",EDGE,"E5.bottom"),sQuery(id+"F0.wireOp",EDGE,"E5.top"),sQuery(id+"F0.wireOp",EDGE,"E5.left"),sQuery(id+"F0.wireOp",EDGE,"E5.right"),sQuery(id+"F0.wireOp",EDGE,"E6.trimOffspring"),sQuery(id+"F0.wireOp",EDGE,"E7.filletArc"),sQuery(id+"F0.wireOp",EDGE,"E8.filletArc"),sQuery(id+"F0.wireOp",EDGE,"E9.filletArc"),sQuery(id+"F0.wireOp",EDGE,"E10.filletArc"),sQuery(id+"F0.wireOp",EDGE,"E11.filletArc"),sQuery(id+"F0.wireOp",EDGE,"E12.filletArc"),sQuery(id+"F0.wireOp",EDGE,"E13.filletArc"),sQuery(id+"F0.wireOp",EDGE,"E14.filletArc"),sQuery(id+"F0.wireOp",EDGE,"E15.filletArc")])],"isStart":false});
            var Q1;
            Q1=makeQuery(id+"F2.opExtrude","CAP_FACE",FACE,{"disambiguationData":[OSD([sQuery(id+"F0.wireOp",EDGE,"E16.bottom"),sQuery(id+"F0.wireOp",EDGE,"E16.top"),sQuery(id+"F0.wireOp",EDGE,"E16.left"),sQuery(id+"F0.wireOp",EDGE,"E16.right")])],"isStart":false});
            var Q2;
            Q2=makeQuery(id+"F2.opExtrude","CAP_FACE",FACE,{"disambiguationData":[OSD([sQuery(id+"F0.wireOp",EDGE,"E17.bottom"),sQuery(id+"F0.wireOp",EDGE,"E17.top"),sQuery(id+"F0.wireOp",EDGE,"E17.left"),sQuery(id+"F0.wireOp",EDGE,"E17.right"),sQuery(id+"F0.wireOp",EDGE,"E18.bottom"),sQuery(id+"F0.wireOp",EDGE,"E18.top"),sQuery(id+"F0.wireOp",EDGE,"E18.left"),sQuery(id+"F0.wireOp",EDGE,"E19.trimOffspring"),sQuery(id+"F0.wireOp",EDGE,"E20.trimOffspring"),sQuery(id+"F0.wireOp",EDGE,"E21.trimOffspring"),sQuery(id+"F0.wireOp",EDGE,"E22.trimOffspring"),sQuery(id+"F0.wireOp",EDGE,"E23"),sQuery(id+"F0.wireOp",EDGE,"E24"),sQuery(id+"F0.wireOp",EDGE,"E25"),sQuery(id+"F0.wireOp",EDGE,"E26"),sQuery(id+"F0.wireOp",EDGE,"E27"),sQuery(id+"F0.wireOp",EDGE,"E28")])],"isStart":false});
            var Q3;
            Q3=makeQuery(id+"F2.opExtrude","CAP_FACE",FACE,{"disambiguationData":[OSD([sQuery(id+"F0.wireOp",EDGE,"E29.bottom"),sQuery(id+"F0.wireOp",EDGE,"E29.top"),sQuery(id+"F0.wireOp",EDGE,"E29.left"),sQuery(id+"F0.wireOp",EDGE,"E29.right")])],"isStart":false});
            var Q4;
            Q4=makeQuery(id+"F2.opExtrude","CAP_FACE",FACE,{"disambiguationData":[OSD([sQuery(id+"F0.wireOp",EDGE,"E30.bottom"),sQuery(id+"F0.wireOp",EDGE,"E30.top"),sQuery(id+"F0.wireOp",EDGE,"E30.left"),sQuery(id+"F0.wireOp",EDGE,"E30.right"),sQuery(id+"F0.wireOp",EDGE,"E31.filletArc"),sQuery(id+"F0.wireOp",EDGE,"E32.filletArc"),sQuery(id+"F0.wireOp",EDGE,"E33"),sQuery(id+"F0.wireOp",EDGE,"E34"),sQuery(id+"F0.wireOp",EDGE,"E35.bottom"),sQuery(id+"F0.wireOp",EDGE,"E35.top"),sQuery(id+"F0.wireOp",EDGE,"E35.left"),sQuery(id+"F0.wireOp",EDGE,"E35.right"),sQuery(id+"F0.wireOp",EDGE,"E36.filletArc"),sQuery(id+"F0.wireOp",EDGE,"E37.filletArc"),sQuery(id+"F0.wireOp",EDGE,"E38.filletArc"),sQuery(id+"F0.wireOp",EDGE,"E39.filletArc"),sQuery(id+"F0.wireOp",EDGE,"E40"),sQuery(id+"F0.wireOp",EDGE,"E41.trimOffspring"),sQuery(id+"F0.wireOp",EDGE,"E42.filletArc"),sQuery(id+"F0.wireOp",EDGE,"E43"),sQuery(id+"F0.wireOp",EDGE,"E44"),sQuery(id+"F0.wireOp",EDGE,"E45.filletArc"),sQuery(id+"F0.wireOp",EDGE,"E79.left")])],"isStart":false});
            var Q5;
            Q5=makeQuery(id+"F2.opExtrude","CAP_FACE",FACE,{"disambiguationData":[OSD([sQuery(id+"F0.wireOp",EDGE,"E46.bottom"),sQuery(id+"F0.wireOp",EDGE,"E46.top"),sQuery(id+"F0.wireOp",EDGE,"E46.left"),sQuery(id+"F0.wireOp",EDGE,"E46.right"),sQuery(id+"F0.wireOp",EDGE,"E47.filletArc"),sQuery(id+"F0.wireOp",EDGE,"E48.filletArc"),sQuery(id+"F0.wireOp",EDGE,"E49.filletArc"),sQuery(id+"F0.wireOp",EDGE,"E50.filletArc"),sQuery(id+"F0.wireOp",EDGE,"E51"),sQuery(id+"F0.wireOp",EDGE,"E52"),sQuery(id+"F0.wireOp",EDGE,"E53"),sQuery(id+"F0.wireOp",EDGE,"E54"),sQuery(id+"F0.wireOp",EDGE,"E55"),sQuery(id+"F0.wireOp",EDGE,"E56"),sQuery(id+"F0.wireOp",EDGE,"E57"),sQuery(id+"F0.wireOp",EDGE,"DLBRGIPo-igv8-U5Ki-hssD-qP5Wvc2arMu2"),sQuery(id+"F0.wireOp",EDGE,"E59"),sQuery(id+"F0.wireOp",EDGE,"E60"),sQuery(id+"F0.wireOp",EDGE,"E61.trimOffspring"),sQuery(id+"F0.wireOp",EDGE,"E62.filletArc"),sQuery(id+"F0.wireOp",EDGE,"E63.filletArc"),sQuery(id+"F0.wireOp",EDGE,"E64.trimOffspring"),sQuery(id+"F0.wireOp",EDGE,"E65.filletArc"),sQuery(id+"F0.wireOp",EDGE,"E66.filletArc")])],"isStart":false});
            var Q6;
            Q6=makeQuery(id+"F2.opExtrude","CAP_FACE",FACE,{"disambiguationData":[OSD([sQuery(id+"F0.wireOp",EDGE,"E67.bottom"),sQuery(id+"F0.wireOp",EDGE,"E67.top"),sQuery(id+"F0.wireOp",EDGE,"E67.left"),sQuery(id+"F0.wireOp",EDGE,"E67.right"),sQuery(id+"F0.wireOp",EDGE,"E68.bottom"),sQuery(id+"F0.wireOp",EDGE,"E68.top"),sQuery(id+"F0.wireOp",EDGE,"W34rrdPF-5A4v-98ez-cMOX-sxhZx3srIAKQ"),sQuery(id+"F0.wireOp",EDGE,"yoT0j4jh-KsDp-Vx2W-hgaE-VbdXvh3J3yn9"),sQuery(id+"F0.wireOp",EDGE,"E69"),sQuery(id+"F0.wireOp",EDGE,"E93.trimOffspring"),sQuery(id+"F0.wireOp",EDGE,"E70"),sQuery(id+"F0.wireOp",EDGE,"FAs5oKjp-0fME-HACK-cPX3-1Olh0WYhMQdt"),sQuery(id+"F0.wireOp",EDGE,"E71.filletArc"),sQuery(id+"F0.wireOp",EDGE,"E72.filletArc"),sQuery(id+"F0.wireOp",EDGE,"E73.filletArc"),sQuery(id+"F0.wireOp",EDGE,"E74.filletArc"),sQuery(id+"F0.wireOp",EDGE,"E75.filletArc"),sQuery(id+"F0.wireOp",EDGE,"E76"),sQuery(id+"F0.wireOp",EDGE,"E77"),sQuery(id+"F0.wireOp",EDGE,"E78")])],"isStart":false});
            fillet(context, id + "F4", {"entities" : qUnion([Q0, Q1, Q2, Q3, Q4, Q5, Q6]), "radius" : .5 * mm, "tangentPropagation" : true, "allowEdgeOverflow" : false});
        }
        {
            var Q0;
            {var subQ0=sQuery(id+"F0.wireOp",EDGE,"E67.left");var subQ1=sQuery(id+"F0.wireOp",EDGE,"E99.trimOffspring");var subQ2=sQuery(id+"F0.wireOp",EDGE,"E64.trimOffspring");var subQ3=sQuery(id+"F0.wireOp",EDGE,"E47.filletArc");var subQ4=sQuery(id+"F0.wireOp",EDGE,"E46.right");var subQ5=sQuery(id+"F0.wireOp",EDGE,"E79.left");var subQ6=sQuery(id+"F0.wireOp",EDGE,"E45.filletArc");var subQ7=sQuery(id+"F0.wireOp",EDGE,"E44");var subQ8=sQuery(id+"F0.wireOp",EDGE,"E43");var subQ9=sQuery(id+"F0.wireOp",EDGE,"E29.right");var subQ10=sQuery(id+"F0.wireOp",EDGE,"E29.left");var subQ11=sQuery(id+"F0.wireOp",EDGE,"E27");var subQ12=sQuery(id+"F0.wireOp",EDGE,"E18.left");var subQ13=sQuery(id+"F0.wireOp",EDGE,"E16.right");var subQ14=sQuery(id+"F0.wireOp",EDGE,"E16.left");var subQ15=sQuery(id+"F0.wireOp",EDGE,"E0.right");Q0=makeQuery(id+"F3.opBoolean","MERGE",FACE,{"derivedFrom":[makeQuery(id+"F1.opExtrude","CAP_FACE",FACE,{"disambiguationData":[OSD([subQ15,subQ14,sQuery(id+"F0.wireOp",EDGE,"E86.trimOffspring"),sQuery(id+"F0.wireOp",EDGE,"E87.trimOffspring")])],"isStart":true}),makeQuery(id+"F1.opExtrude","CAP_FACE",FACE,{"disambiguationData":[OSD([subQ13,subQ11,sQuery(id+"F0.wireOp",EDGE,"E82"),sQuery(id+"F0.wireOp",EDGE,"E83"),sQuery(id+"F0.wireOp",EDGE,"E84"),sQuery(id+"F0.wireOp",EDGE,"E85")])],"isStart":true}),makeQuery(id+"F1.opExtrude","CAP_FACE",FACE,{"disambiguationData":[OSD([subQ12,subQ10,sQuery(id+"F0.wireOp",EDGE,"E80.trimOffspring"),sQuery(id+"F0.wireOp",EDGE,"E81.trimOffspring")])],"isStart":true}),makeQuery(id+"F1.opExtrude","CAP_FACE",FACE,{"disambiguationData":[OSD([subQ9,sQuery(id+"F0.wireOp",EDGE,"E79.bottom"),sQuery(id+"F0.wireOp",EDGE,"E79.top"),subQ5])],"isStart":true}),makeQuery(id+"F1.opExtrude","CAP_FACE",FACE,{"disambiguationData":[OSD([subQ8,subQ7,subQ6,subQ4,subQ3,subQ1,sQuery(id+"F0.wireOp",EDGE,"E119"),sQuery(id+"F0.wireOp",EDGE,"E120")])],"isStart":true}),makeQuery(id+"F1.opExtrude","CAP_FACE",FACE,{"disambiguationData":[OSD([subQ2,subQ0,sQuery(id+"F0.wireOp",EDGE,"E121"),sQuery(id+"F0.wireOp",EDGE,"E122")])],"isStart":true}),makeQuery(id+"F2.opExtrude","CAP_FACE",FACE,{"disambiguationData":[OSD([sQuery(id+"F0.wireOp",EDGE,"E0.bottom"),sQuery(id+"F0.wireOp",EDGE,"E0.top"),sQuery(id+"F0.wireOp",EDGE,"E0.left"),subQ15,sQuery(id+"F0.wireOp",EDGE,"E1.filletArc"),sQuery(id+"F0.wireOp",EDGE,"E2"),sQuery(id+"F0.wireOp",EDGE,"E3"),sQuery(id+"F0.wireOp",EDGE,"E4"),sQuery(id+"F0.wireOp",EDGE,"E5.bottom"),sQuery(id+"F0.wireOp",EDGE,"E5.top"),sQuery(id+"F0.wireOp",EDGE,"E5.left"),sQuery(id+"F0.wireOp",EDGE,"E5.right"),sQuery(id+"F0.wireOp",EDGE,"E6.trimOffspring"),sQuery(id+"F0.wireOp",EDGE,"E7.filletArc"),sQuery(id+"F0.wireOp",EDGE,"E8.filletArc"),sQuery(id+"F0.wireOp",EDGE,"E9.filletArc"),sQuery(id+"F0.wireOp",EDGE,"E10.filletArc"),sQuery(id+"F0.wireOp",EDGE,"E11.filletArc"),sQuery(id+"F0.wireOp",EDGE,"E12.filletArc"),sQuery(id+"F0.wireOp",EDGE,"E13.filletArc"),sQuery(id+"F0.wireOp",EDGE,"E14.filletArc"),sQuery(id+"F0.wireOp",EDGE,"E15.filletArc")])],"isStart":true}),makeQuery(id+"F2.opExtrude","CAP_FACE",FACE,{"disambiguationData":[OSD([sQuery(id+"F0.wireOp",EDGE,"E16.bottom"),sQuery(id+"F0.wireOp",EDGE,"E16.top"),subQ14,subQ13])],"isStart":true}),makeQuery(id+"F2.opExtrude","CAP_FACE",FACE,{"disambiguationData":[OSD([sQuery(id+"F0.wireOp",EDGE,"E17.bottom"),sQuery(id+"F0.wireOp",EDGE,"E17.top"),sQuery(id+"F0.wireOp",EDGE,"E17.left"),sQuery(id+"F0.wireOp",EDGE,"E17.right"),sQuery(id+"F0.wireOp",EDGE,"E18.bottom"),sQuery(id+"F0.wireOp",EDGE,"E18.top"),subQ12,sQuery(id+"F0.wireOp",EDGE,"E19.trimOffspring"),sQuery(id+"F0.wireOp",EDGE,"E20.trimOffspring"),sQuery(id+"F0.wireOp",EDGE,"E21.trimOffspring"),sQuery(id+"F0.wireOp",EDGE,"E22.trimOffspring"),sQuery(id+"F0.wireOp",EDGE,"E23"),sQuery(id+"F0.wireOp",EDGE,"E24"),sQuery(id+"F0.wireOp",EDGE,"E25"),sQuery(id+"F0.wireOp",EDGE,"E26"),subQ11,sQuery(id+"F0.wireOp",EDGE,"E28")])],"isStart":true}),makeQuery(id+"F2.opExtrude","CAP_FACE",FACE,{"disambiguationData":[OSD([sQuery(id+"F0.wireOp",EDGE,"E29.bottom"),sQuery(id+"F0.wireOp",EDGE,"E29.top"),subQ10,subQ9])],"isStart":true}),makeQuery(id+"F2.opExtrude","CAP_FACE",FACE,{"disambiguationData":[OSD([sQuery(id+"F0.wireOp",EDGE,"E30.bottom"),sQuery(id+"F0.wireOp",EDGE,"E30.top"),sQuery(id+"F0.wireOp",EDGE,"E30.left"),sQuery(id+"F0.wireOp",EDGE,"E30.right"),sQuery(id+"F0.wireOp",EDGE,"E31.filletArc"),sQuery(id+"F0.wireOp",EDGE,"E32.filletArc"),sQuery(id+"F0.wireOp",EDGE,"E33"),sQuery(id+"F0.wireOp",EDGE,"E34"),sQuery(id+"F0.wireOp",EDGE,"E35.bottom"),sQuery(id+"F0.wireOp",EDGE,"E35.top"),sQuery(id+"F0.wireOp",EDGE,"E35.left"),sQuery(id+"F0.wireOp",EDGE,"E35.right"),sQuery(id+"F0.wireOp",EDGE,"E36.filletArc"),sQuery(id+"F0.wireOp",EDGE,"E37.filletArc"),sQuery(id+"F0.wireOp",EDGE,"E38.filletArc"),sQuery(id+"F0.wireOp",EDGE,"E39.filletArc"),sQuery(id+"F0.wireOp",EDGE,"E40"),sQuery(id+"F0.wireOp",EDGE,"E41.trimOffspring"),sQuery(id+"F0.wireOp",EDGE,"E42.filletArc"),subQ8,subQ7,subQ6,subQ5])],"isStart":true}),makeQuery(id+"F2.opExtrude","CAP_FACE",FACE,{"disambiguationData":[OSD([sQuery(id+"F0.wireOp",EDGE,"E46.bottom"),sQuery(id+"F0.wireOp",EDGE,"E46.top"),sQuery(id+"F0.wireOp",EDGE,"E46.left"),subQ4,subQ3,sQuery(id+"F0.wireOp",EDGE,"E48.filletArc"),sQuery(id+"F0.wireOp",EDGE,"E49.filletArc"),sQuery(id+"F0.wireOp",EDGE,"E50.filletArc"),sQuery(id+"F0.wireOp",EDGE,"E51"),sQuery(id+"F0.wireOp",EDGE,"E52"),sQuery(id+"F0.wireOp",EDGE,"E53"),sQuery(id+"F0.wireOp",EDGE,"E54"),sQuery(id+"F0.wireOp",EDGE,"E55"),sQuery(id+"F0.wireOp",EDGE,"E56"),sQuery(id+"F0.wireOp",EDGE,"E57"),sQuery(id+"F0.wireOp",EDGE,"E59"),sQuery(id+"F0.wireOp",EDGE,"E60"),sQuery(id+"F0.wireOp",EDGE,"E62.filletArc"),sQuery(id+"F0.wireOp",EDGE,"E63.filletArc"),subQ2,sQuery(id+"F0.wireOp",EDGE,"E65.filletArc"),sQuery(id+"F0.wireOp",EDGE,"E66.filletArc"),sQuery(id+"F0.wireOp",EDGE,"E90"),subQ1,sQuery(id+"F0.wireOp",EDGE,"E100.trimOffspring"),sQuery(id+"F0.wireOp",EDGE,"E101.trimOffspring"),sQuery(id+"F0.wireOp",EDGE,"E102.trimOffspring"),sQuery(id+"F0.wireOp",EDGE,"E103.trimOffspring"),sQuery(id+"F0.wireOp",EDGE,"E104.trimOffspring"),sQuery(id+"F0.wireOp",EDGE,"E109"),sQuery(id+"F0.wireOp",EDGE,"E110"),sQuery(id+"F0.wireOp",EDGE,"E111"),sQuery(id+"F0.wireOp",EDGE,"E112"),sQuery(id+"F0.wireOp",EDGE,"E113"),sQuery(id+"F0.wireOp",EDGE,"E114")])],"isStart":true}),makeQuery(id+"F2.opExtrude","CAP_FACE",FACE,{"disambiguationData":[OSD([sQuery(id+"F0.wireOp",EDGE,"E67.bottom"),sQuery(id+"F0.wireOp",EDGE,"E67.top"),subQ0,sQuery(id+"F0.wireOp",EDGE,"E68.bottom"),sQuery(id+"F0.wireOp",EDGE,"E68.top"),sQuery(id+"F0.wireOp",EDGE,"E69"),sQuery(id+"F0.wireOp",EDGE,"E70"),sQuery(id+"F0.wireOp",EDGE,"E72.filletArc"),sQuery(id+"F0.wireOp",EDGE,"E73.filletArc"),sQuery(id+"F0.wireOp",EDGE,"E74.filletArc"),sQuery(id+"F0.wireOp",EDGE,"E75.filletArc"),sQuery(id+"F0.wireOp",EDGE,"E76"),sQuery(id+"F0.wireOp",EDGE,"E77"),sQuery(id+"F0.wireOp",EDGE,"E78"),sQuery(id+"F0.wireOp",EDGE,"E91.top"),sQuery(id+"F0.wireOp",EDGE,"E92"),sQuery(id+"F0.wireOp",EDGE,"E94"),sQuery(id+"F0.wireOp",EDGE,"E95"),sQuery(id+"F0.wireOp",EDGE,"E96"),sQuery(id+"F0.wireOp",EDGE,"E97.filletArc"),sQuery(id+"F0.wireOp",EDGE,"E98.filletArc"),sQuery(id+"F0.wireOp",EDGE,"E105.trimOffspring"),sQuery(id+"F0.wireOp",EDGE,"E106.trimOffspring"),sQuery(id+"F0.wireOp",EDGE,"E107.trimOffspring"),sQuery(id+"F0.wireOp",EDGE,"E108.trimOffspring"),sQuery(id+"F0.wireOp",EDGE,"E115"),sQuery(id+"F0.wireOp",EDGE,"E116"),sQuery(id+"F0.wireOp",EDGE,"E117"),sQuery(id+"F0.wireOp",EDGE,"E118")])],"isStart":true})]});}
            var sketch = newSketch(context, id + "F5", { "sketchPlane" : qUnion([Q0])});
            skCircle(sketch, "E123", {"center": v(-52.37, 23.22) * mm, "radius": 2 * mm});
            skCircle(sketch, "E124", {"center": v(-45.8, 18.36) * mm, "radius": 2 * mm});
            skCircle(sketch, "E125", {"center": v(-25.99, 22.84) * mm, "radius": 2 * mm});
            skCircle(sketch, "E126", {"center": v(-6.34, 28.97) * mm, "radius": 2 * mm});
            skCircle(sketch, "E127", {"center": v(13.77, 26.59) * mm, "radius": 2 * mm});
            skCircle(sketch, "E128", {"center": v(40.41, 26.68) * mm, "radius": 2 * mm});
            skCircle(sketch, "E129", {"center": v(65.88, 30.92) * mm, "radius": 2 * mm});
            skSolve(sketch);
        }
        {
            var Q0;
            Q0 = qSketchRegion(id + "F5", true);
            extrude(context, id + "F6", {"entities" : qUnion([Q0]), "operationType" : NewBodyOperationType.REMOVE, "oppositeDirection" : true, "depth" : 1 * mm, "offsetDistance" : 25 * mm});
        }
    });
